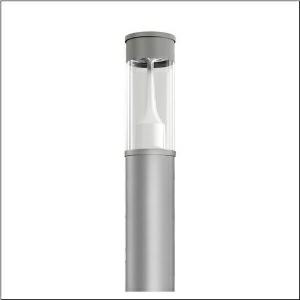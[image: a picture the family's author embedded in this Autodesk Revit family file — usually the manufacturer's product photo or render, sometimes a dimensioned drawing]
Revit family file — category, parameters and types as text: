
# Revit family: city-light_400_iq___p1_0a_5xa5305lf14hp_1a81
name_source: partatom
category: Lighting Fixtures
units: mm (PartAtom-declared; Revit-internal decimal feet)

## family parameters
Cut with Voids When Loaded = No
Host = Face
Light Source = No
Part Type = Normal
Room Calculation Point = No
Round Connector Dimension = Use Diameter
Shared = No

## types (1)
- --- (1 x LED, 4910 lm, 33.6 W, 4000K)
    Apparent Load = 34 VA
    CIE Flux Codes = 31 62 91 95 100
    Color Rendering = 70
    Color Temperature = 4000K
    Default Elevation = 1800 mm
    Description = City-Light 400 iQ, light pillar, Module 540 iQ-SR, primary light control with 3 zone facetted reflector, of plastic, silver coated, highly specular, structured, primary optical cover: cover, of PMMA, transparent, partly coated, light distribution: P1.0a, primary light characteristic: strongly asymmetric, LED, High Power LED, rated luminous flux: 4.910lm, luminous efficacy: 146lm/W, light colour: 740, colour temperature: 4000K, control gear: iQ Street-Remote, control: pre-setting: logarithmic dimming characteristic, Street-Remote, Auto-Match, Temp-Guard, Lumen-Switch, Night-Set, Smart-Wire, Light-Fading, Desk-Remote (wireless, voltage-free reading and setting of iQ features in the workshop via application-optimized NFC function/RFID function), optimised constant luminous flux control (CLO 2.0), with terminal, 6-pole, max. 2.5mm², mains connection: 230..240V, AC, 50/60Hz, start of lifetime: 34W, end of service life: 36W, reduction: 15W, luminaire housing, cylindrical, of extruded aluminium section, coated, Siteco® metallic grey (DB 702S), length: 4.694mm, diameter: 200mm, Module 540 iQ-SR, traffic white (RAL 9016), equipment: Power, protection rating (complete): IP65, insulation class (complete): insulation class II (safety insulation), certification: CE, ENEC, VDE, packaging unit: 1 piece

Light Distribution: P1.0a
    Height = 500 mm
    Lamp = 1 x LED
    Lamp Light Flux = 4910 lm
    Lamp Power = 33.6 W
    Lamp count = 1
    Length = 200 mm  [stored 0.656168 ft]
    Luminous efficacy = 146 lm/W
    Manufacturer = Siteco
    ModVariant = No
    Model = 5XA5305LF14HP
    Mounting Place = Floor
    Mounting Type = Freestanding
    Number of Poles = 1
    OnlyDefault = Yes
    Power Factor = 1
    Product Name = City-Light 400 iQ | P1.0a
    Product group = light pillar
    ProductGroupID = 1301
    Protection Class = Protection class II
    Protection Degree = IP 65
    RLX_Detail_Level = 1
    RLX_Emergency_Light_Flux = 0 lm
    RLX_Emergency_Type = 0
    RLX_Emergency_Type_DB = No
    RlxData = <blob elided: 53693 chars, md5=6e022219>
    Socket = socket
    Standby Power = 0 W
    System Light Flux = 4910 lm
    System Power = 34 W
    Type Comments = factory setting: luminous flux: 100 % | dim-lin: 254 | 695 mA
    Type Image = l_1006916.jpg
    URL = http://relux.com
    VarID = @adj_192708
    Voltage = 0 V
    Weight = 0.00 kg
    Width = 0 mm  [stored 0 ft]

note: [stored X ft] marks values corroborated as IEEE doubles in the binary element streams (Revit-internal decimal feet)

## geometry (parser evidence)
native form markers: Blend x4, Sweep x9
no freeform markers — native parametric forms only
